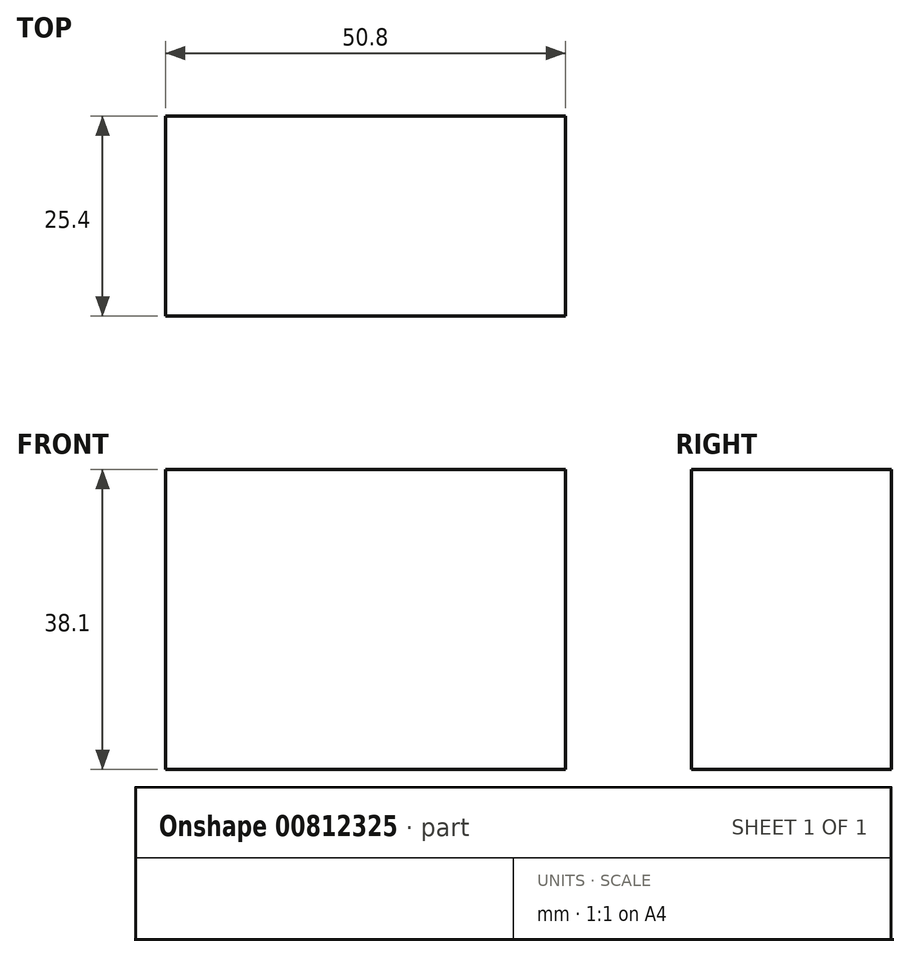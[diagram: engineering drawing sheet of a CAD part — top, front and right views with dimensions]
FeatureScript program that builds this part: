
annotation { "Feature Type Name" : "Feature", "Feature Type Description" : "" }
export const myFeature = defineFeature(function(context is Context, id is Id, definition is map)
    precondition{}
    {
        {
            var Q0;
            Q0=qCreatedBy(makeId("Front.planeOp"),FACE);
            var sketch = newSketch(context, id + "F0", { "sketchPlane" : qUnion([Q0])});
            skLineSegment(sketch, "E0.bottom", {"start": v(0, 0) * mm, "end": v(50.8, 0) * mm});
            skLineSegment(sketch, "E0.top", {"start": v(0, 38.1) * mm, "end": v(50.8, 38.1) * mm});
            skLineSegment(sketch, "E0.left", {"start": v(0, 0) * mm, "end": v(0, 38.1) * mm});
            skLineSegment(sketch, "E0.right", {"start": v(50.8, 0) * mm, "end": v(50.8, 38.1) * mm});
            skSolve(sketch);
        }
        {
            var Q0;
            Q0=makeQuery(id+"F0.imprint","IMPRINT",FACE,{"disambiguationData":[TD([[makeQuery(id+"F0.imprint","IMPRINT",EDGE,{"derivedFrom":sQuery(id+"F0.wireOp",EDGE,"E0.bottom")}),1.0]])]});
            extrude(context, id + "F1", {"entities" : qUnion([Q0]), "depth" : 25.4 * mm, "offsetDistance" : 25.4 * mm});
        }
    });
